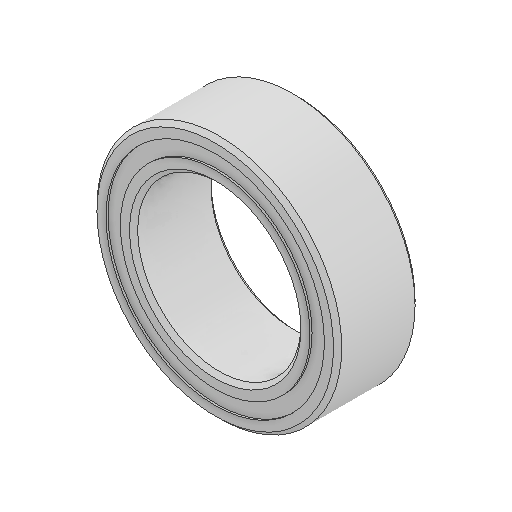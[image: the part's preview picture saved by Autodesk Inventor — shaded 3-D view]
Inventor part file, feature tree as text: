
AUTODESK INVENTOR PART (.ipt)
format: ipt  version: 2024.1 (Build 281209000, 209)  size: 591,360 bytes
history: native  units: in
note: dims shown in document units (in); Inventor stores cm internally (conversion verified against a paired STEP export)
features: other x11, revolve x5
ambient origin geometry x8: Origin, YZ Plane, XZ Plane, XY Plane, X Axis, Y Axis, Z Axis, Center Point
bodies: Solid1 (feature_tree), Solid2 (feature_tree), Solid3 (feature_tree), Solid4 (feature_tree), Solid5 (feature_tree), Solid6 (feature_tree), Solid7 (feature_tree), Solid8 (feature_tree), Solid9 (feature_tree), Solid10 (feature_tree), Solid11 (feature_tree), Solid12 (feature_tree), Solid13 (feature_tree), Solid14 (feature_tree), Solid15 (feature_tree), Solid16 (feature_tree)
feature tree (16):
  revolve  "Revolve1"  [1 undecoded]
  revolve  "Revolve3"  [1 undecoded]
  revolve  "Revolve4"  [1 undecoded]
  other  "CirPattern1[1]"
  other  "CirPattern1[2]"
  other  "CirPattern1[3]"
  other  "CirPattern1[4]"
  other  "CirPattern1[5]"
  other  "CirPattern1[6]"
  other  "CirPattern1[7]"
  other  "CirPattern1[8]"
  other  "CirPattern1[9]"
  other  "CirPattern1[10]"
  other  "CirPattern1[11]"
  revolve  "Revolve5[1]"  [1 undecoded]
  revolve  "Revolve5[2]"  [1 undecoded]
note: 5 required parameter values undecoded (feature->parameter linkage not recoverable at this tier; creation-order binding heuristic only, values carry confidence <= 0.55)
